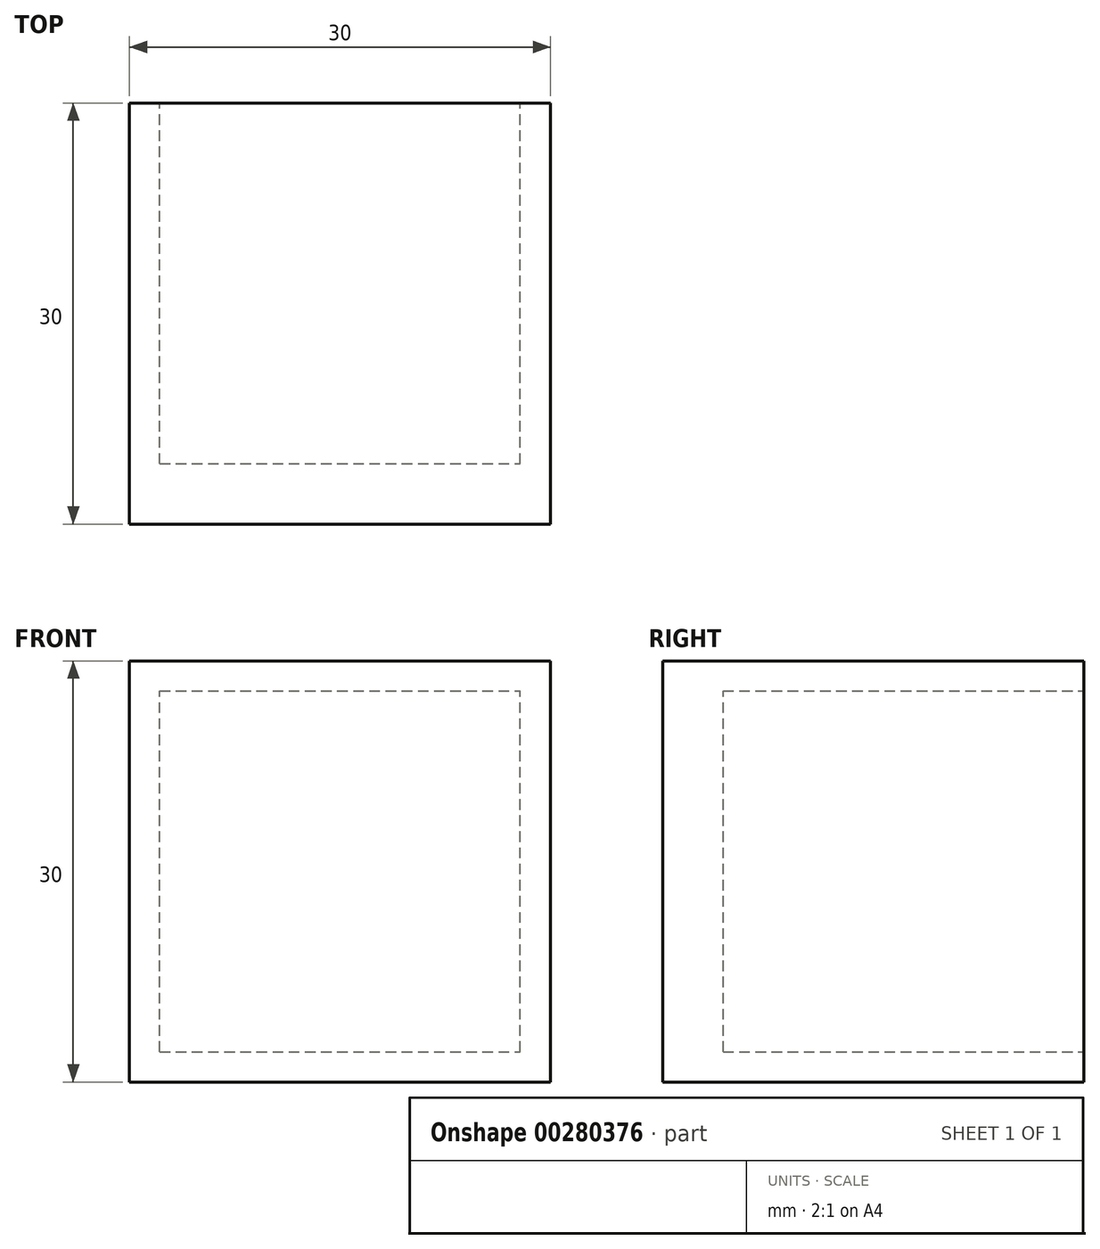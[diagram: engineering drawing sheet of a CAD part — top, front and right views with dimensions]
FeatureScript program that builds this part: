
annotation { "Feature Type Name" : "Feature", "Feature Type Description" : "" }
export const myFeature = defineFeature(function(context is Context, id is Id, definition is map)
    precondition{}
    {
        {
            var Q0;
            Q0=qCreatedBy(makeId("Front.planeOp"),FACE);
            var sketch = newSketch(context, id + "F0", { "sketchPlane" : qUnion([Q0])});
            skLineSegment(sketch, "E0.bottom", {"start": v(15, -15) * mm, "end": v(-15, -15) * mm});
            skLineSegment(sketch, "E0.top", {"start": v(15, 15) * mm, "end": v(-15, 15) * mm});
            skLineSegment(sketch, "E0.left", {"start": v(15, -15) * mm, "end": v(15, 15) * mm});
            skLineSegment(sketch, "E0.right", {"start": v(-15, -15) * mm, "end": v(-15, 15) * mm});
            skPoint(sketch, "E0.middle", {"position": v(0, 0) * mm});
            skSolve(sketch);
        }
        {
            var Q0;
            Q0 = qSketchRegion(id + "F0", true);
            extrude(context, id + "F1", {"entities" : qUnion([Q0]), "depth" : 30 * mm});
        }
        {
            var Q0;
            Q0=qCreatedBy(makeId("Front.planeOp"),FACE);
            var sketch = newSketch(context, id + "F2", { "sketchPlane" : qUnion([Q0])});
            skLineSegment(sketch, "E1.bottom", {"start": v(-12.85, -12.85) * mm, "end": v(12.85, -12.85) * mm});
            skLineSegment(sketch, "E1.top", {"start": v(-12.85, 12.85) * mm, "end": v(12.85, 12.85) * mm});
            skLineSegment(sketch, "E1.left", {"start": v(-12.85, -12.85) * mm, "end": v(-12.85, 12.85) * mm});
            skLineSegment(sketch, "E1.right", {"start": v(12.85, -12.85) * mm, "end": v(12.85, 12.85) * mm});
            skPoint(sketch, "E1.middle", {"position": v(0, 0) * mm});
            skSolve(sketch);
        }
        {
            var Q0;
            Q0=makeQuery(id+"F2.imprint","IMPRINT",FACE,{"disambiguationData":[TD([[makeQuery(id+"F2.imprint","IMPRINT",EDGE,{"derivedFrom":sQuery(id+"F2.wireOp",EDGE,"E1.bottom")}),1.0]])]});
            extrude(context, id + "F3", {"entities" : qUnion([Q0]), "operationType" : NewBodyOperationType.REMOVE, "depth" : 25.7 * mm});
        }
    });
